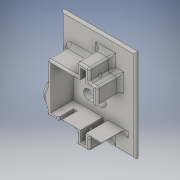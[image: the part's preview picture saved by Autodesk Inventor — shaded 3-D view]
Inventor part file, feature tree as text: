
AUTODESK INVENTOR PART (.ipt)
format: ipt  version: 2016 (Build 200138000, 138)  size: 625,664 bytes
history: native  units: in
note: dims shown in document units (in); Inventor stores cm internally (conversion verified against a paired STEP export)
features: sketch x10, fillet x8, extrude x6, hole x1
ambient origin geometry x8: Origin, YZ Plane, XZ Plane, XY Plane, X Axis, Y Axis, Z Axis, Center Point
bodies: Solid1 (feature_tree)
feature tree (25):
  extrude  "Extrusion1"  Depth=0.1181in
  fillet  "Fillet1"  Radius=0.1575in
  fillet  "Fillet2"  Radius=0.0394in
  extrude  "Extrusion4"  Depth=0.1063in
  extrude  "Extrusion5"  Depth=0.6142in
  hole  "Hole3"  [1 undecoded]
  fillet  "Fillet8"  Radius=0.1654in
  fillet  "Fillet9"  Radius=0.2992in
  extrude  "Extrusion6"  Depth=0.2165in
  sketch  "Sketch20"  dims[d92=0.2165in d93=0.2165in]
  sketch  "Sketch21"  dims[d95=0.9016in d97=0.0787in d98=0.0787in d99=0.0787in d100=0.0787in d101=0.0787in]
  extrude  "Extrusion7"  Depth=0.0787in
  fillet  "Fillet13"  Radius=0.0787in
  fillet  "Fillet14"  Radius=0.0787in
  fillet  "Fillet15"  Radius=0.0787in
  fillet  "Fillet16"  Radius=0.0787in
  sketch  "Sketch23"  dims[d105=0.0787in]
  extrude  "Extrusion8"  Depth=0.1693in
  sketch  "Sketch1"  dims[d2=0.1181in d3=0.0in d6=0.8976in d9=0.357in d10=0.7139in]
  sketch  "Sketch12"  dims[d11=0.0787in d12=0.0787in d13=0.0787in d14=0.0787in d45=0.1575in d46=0.0394in]
  sketch  "Sketch14"  dims[d82=0.9016in d83=0.8858in d85=0.1063in]
  sketch  "Sketch17"  dims[d86=0.1063in d87=0.6142in]
  sketch  "Sketch18"  dims[d88=0.6142in d89=0.1654in d90=0.1654in d91=0.2992in]
  sketch  "Sketch22"  dims[d102=0.0787in d103=0.1693in]
  sketch  "Sketch24"  dims[d106=0.0394in d107=0.0394in d108=0.0394in d109=0.0394in d110=0.1575in d111=0.0787in d112=0.0787in d113=0.0394in d114=0.9016in d125=0.0984in d130=0.185in d132=0.3543in d133=0.2165in d134=0.4724in d135=0.0in d136=0.0787in d137=0.315in d138=0.0in d139=0.0787in d144=0.0394in d145=0.7461in d146=0.0394in d147=0.07in d148=0.2362in d149=0.119in d150=0.0787in d151=0.5635in d152=0.315in d153=0.8108in d154=0.0787in d155=0.0394in d156=0.2717in d157=0.2323in d158=0.2835in d159=0.4016in d160=0.1575in d161=0.0in d164=0.2559in d165=0.0394in d166=0.1575in d167=0.0in d169=0.1535in d170=0.0787in d171=0.0787in d172=0.0394in d173=0.1969in d174=0.1969in d178=0.1575in d179=0.1575in d182=0.2756in d183=0.2756in d184=0.2067in d185=0.2067in d186=0.2067in d187=0.3937in d188=0.0in d189=0.2559in d26=0.0394in d27=0.0394in]
note: 1 required parameter value undecoded (feature->parameter linkage not recoverable at this tier; creation-order binding heuristic only, values carry confidence <= 0.55)
